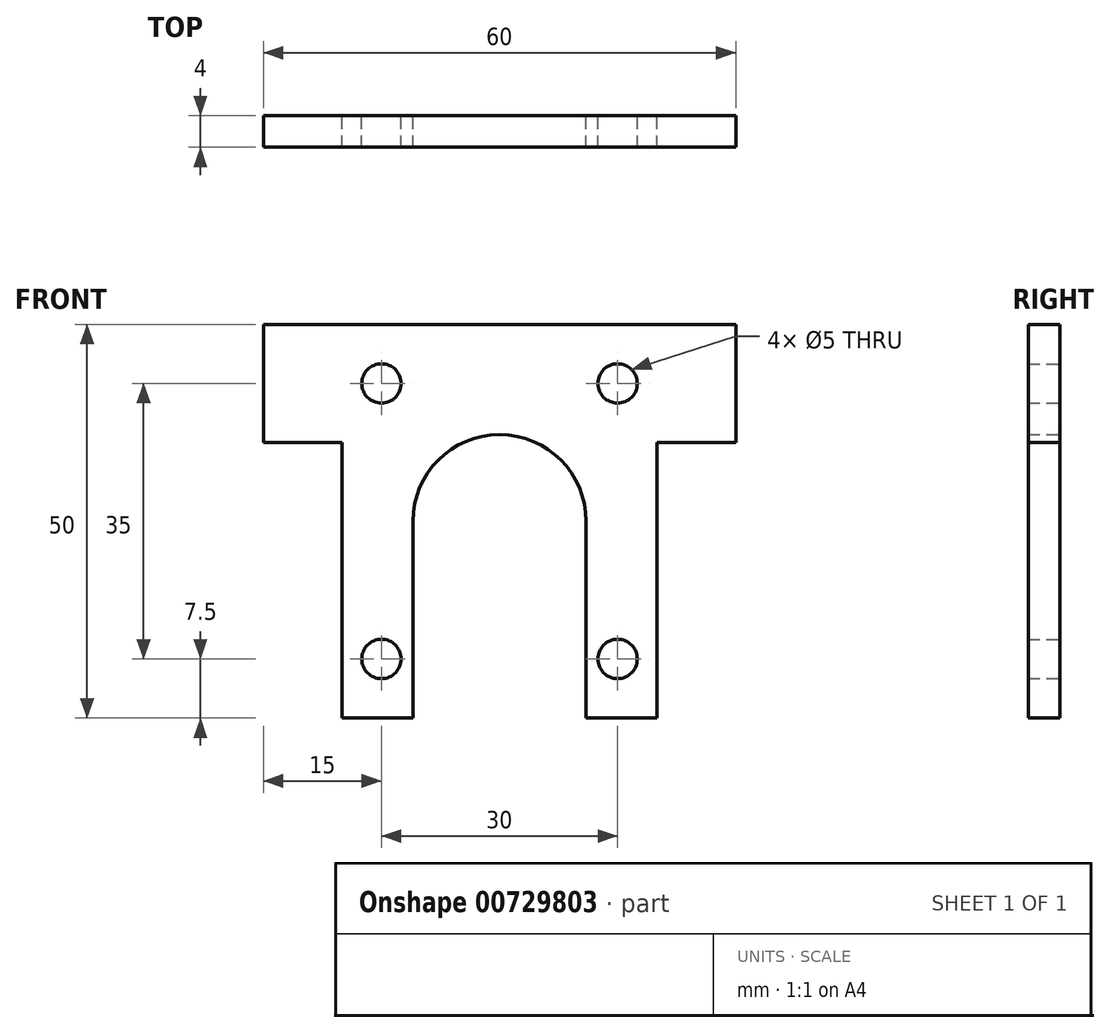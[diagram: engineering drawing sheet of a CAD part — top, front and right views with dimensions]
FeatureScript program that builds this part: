
annotation { "Feature Type Name" : "Feature", "Feature Type Description" : "" }
export const myFeature = defineFeature(function(context is Context, id is Id, definition is map)
    precondition{}
    {
        {
            var Q0;
            Q0=qCreatedBy(makeId("Front.planeOp"),FACE);
            var sketch = newSketch(context, id + "F0", { "sketchPlane" : qUnion([Q0])});
            skArc(sketch, "E0", {"start": v(11, 0) * mm, "mid": v(0, 11) * mm, "end": v(-11, 0) * mm});
            skLineSegment(sketch, "E1.bottom", {"start": v(15, 17.5) * mm, "end": v(-15, 17.5) * mm, "construction": true});
            skLineSegment(sketch, "E1.top", {"start": v(15, -17.5) * mm, "end": v(-15, -17.5) * mm, "construction": true});
            skLineSegment(sketch, "E1.left", {"start": v(15, 17.5) * mm, "end": v(15, -17.5) * mm, "construction": true});
            skLineSegment(sketch, "E1.right", {"start": v(-15, 17.5) * mm, "end": v(-15, -17.5) * mm, "construction": true});
            skCircle(sketch, "E2", {"center": v(-15, 17.5) * mm, "radius": 2.5 * mm});
            skCircle(sketch, "E3", {"center": v(15, 17.5) * mm, "radius": 2.5 * mm});
            skCircle(sketch, "E4", {"center": v(-15, -17.5) * mm, "radius": 2.5 * mm});
            skCircle(sketch, "E5", {"center": v(15, -17.5) * mm, "radius": 2.5 * mm});
            skLineSegment(sketch, "E6", {"start": v(-11, 0) * mm, "end": v(-11, -25) * mm});
            skLineSegment(sketch, "E7", {"start": v(-11, -25) * mm, "end": v(-20, -25) * mm});
            skLineSegment(sketch, "E8", {"start": v(-20, -25) * mm, "end": v(-20, 10) * mm});
            skLineSegment(sketch, "E9", {"start": v(-20, 10) * mm, "end": v(-30, 10) * mm});
            skLineSegment(sketch, "E10", {"start": v(-30, 10) * mm, "end": v(-30, 25) * mm});
            skLineSegment(sketch, "E11", {"start": v(-30, 25) * mm, "end": v(30, 25) * mm});
            skLineSegment(sketch, "E12", {"start": v(30, 25) * mm, "end": v(30, 10) * mm});
            skLineSegment(sketch, "E13", {"start": v(30, 10) * mm, "end": v(20, 10) * mm});
            skLineSegment(sketch, "E14", {"start": v(20, 10) * mm, "end": v(20, -25) * mm});
            skLineSegment(sketch, "E15", {"start": v(20, -25) * mm, "end": v(11, -25) * mm});
            skLineSegment(sketch, "E16", {"start": v(11, -25) * mm, "end": v(11, 0) * mm});
            skSolve(sketch);
        }
        {
            var Q0;
            Q0 = qSketchRegion(id + "F0", true);
            extrude(context, id + "F1", {"entities" : qUnion([Q0]), "depth" : 4 * mm, "offsetDistance" : 25 * mm});
        }
    });
